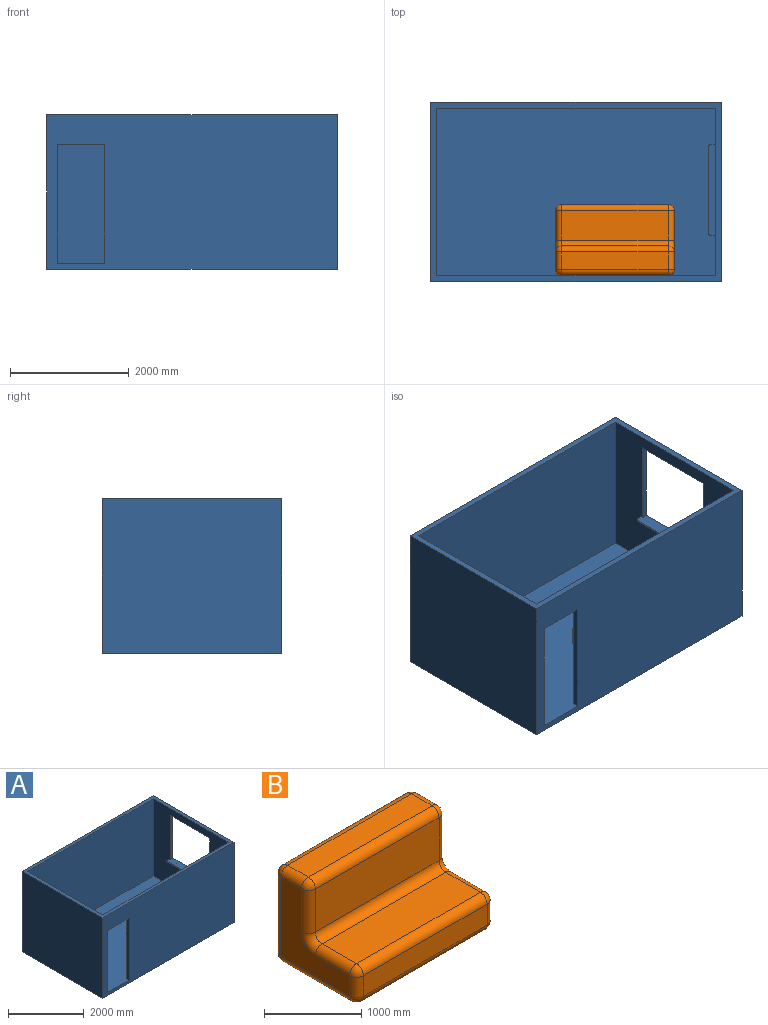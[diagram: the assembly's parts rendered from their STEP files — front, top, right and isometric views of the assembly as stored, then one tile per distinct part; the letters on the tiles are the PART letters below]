
ASSEMBLY  parts=2 mates=2
PART A: 24 faces, bbox 4900x3020x2600 mm
  f0: plane 2820x2500mm, normal (-1,0,0), area 4899320mm2, adj f2,f6,f8,f9,f14,f15,f16,f17
  f1: plane 4900x2600mm, normal (0,-1,0), area 11140000mm2, adj f3,f4,f8,f9,f10,f11,f12,f13
  f2: plane 4700x2500mm, normal (0,1,0), area 10150000mm2, adj f0,f5,f8,f9,f11,f12,f13
  f3: plane 3020x2600mm, normal (-1,0,0), area 7852000mm2, adj f1,f7,f8,f10
  f4: plane 3020x2600mm, normal (1,0,0), area 5735200mm2, adj f1,f7,f8,f10,f14,f15,f16,f17
  f5: plane 2820x2500mm, normal (1,0,0), area 7050000mm2, adj f2,f6,f8,f9
  f6: plane 4700x2500mm, normal (0,-1,0), area 11750000mm2, adj f0,f5,f8,f9
  f7: plane 4900x2600mm, normal (0,1,0), area 12740000mm2, adj f3,f4,f8,f10
  f8: plane 4900x3020mm, normal (0,0,1), area 1544000mm2, adj f0,f1,f2,f3,f4,f5,f6,f7
  f9: plane 4700x2920mm, normal (0,0,1), area 13334000mm2, adj f0,f1,f2,f5,f6,f11,f12
  f10: plane 4900x3020mm, normal (0,0,-1), area 14798000mm2, adj f1,f3,f4,f7
  f11: plane 2000x100mm, normal (1,0,0), area 200000mm2, adj f1,f2,f9,f13
  f12: plane 2000x100mm, normal (-1,0,0), area 200000mm2, adj f1,f2,f9,f13
  f13: plane 800x100mm, normal (0,0,-1), area 80000mm2, adj f1,f2,f11,f12
  f14: plane 1440x100mm, normal (0,-1,0), area 144000mm2, adj f0,f4,f15,f17
  f15: plane 1540x210mm, normal (0,0,1), area 315874.2mm2, adj f0,f4,f14,f16,f18,f20,f21,f22
  f16: plane 1440x100mm, normal (0,1,0), area 144000mm2, adj f0,f4,f15,f17
  f17: plane 1470x100mm, normal (0,0,-1), area 147000mm2, adj f0,f4,f14,f16
  f18: plane 75x22mm, normal (0,1,0), area 1650mm2, adj f0,f15,f19,f22
  f19: plane 1540x110mm, normal (0,0,-1), area 168874.2mm2, adj f0,f18,f20,f21,f22,f23
  f20: plane 75x22mm, normal (0,-1,0), area 1650mm2, adj f0,f15,f19,f23
  f21: plane 1470x22mm, normal (-1,0,0), area 32340mm2, adj f15,f19,f22,f23
  f22: cylinder r=35mm len=35mm, axis (0,0,1), area 1209.5mm2, adj f15,f18,f19,f21
  f23: cylinder r=35mm len=35mm, axis (0,0,-1), area 1209.5mm2, adj f15,f19,f20,f21
PART B: 38 faces, bbox 2000x1200x1200 mm
  f0: plane 1000x1000mm, normal (1,0,0), area 490584.1mm2, adj f8,f12,f13,f22,f23,f24,f28
  f1: plane 1800x300mm, normal (0,0,1), area 540000mm2, adj f11,f12,f20,f21
  f2: plane 1800x260mm, normal (0,-1,0), area 468000mm2, adj f24,f25,f33,f34
  f3: plane 1800x1000mm, normal (0,1,0), area 1800000mm2, adj f8,f11,f14,f15
  f4: plane 1000x1000mm, normal (-1,0,0), area 490584.1mm2, adj f15,f20,f26,f31,f34,f35,f37
  f5: plane 1800x1000mm, normal (0,0,-1), area 1800000mm2, adj f13,f14,f25,f26
  f6: plane 1800x500mm, normal (0,0,1), area 900000mm2, adj f23,f32,f33,f37
  f7: plane 1800x540mm, normal (0,-1,0), area 972000mm2, adj f21,f22,f31,f32
  f8: cylinder r=100mm len=1000mm, axis (0,0,-1), area 157079.6mm2, adj f0,f3,f9,f10
  f9: sphere r=100mm, area 15708mm2, adj f8,f11,f12
  f10: sphere r=100mm, area 15708mm2, adj f8,f13,f14
  f11: cylinder r=100mm len=1800mm, axis (1,0,0), area 282743.3mm2, adj f1,f3,f9,f16
  f12: cylinder r=100mm len=300mm, axis (0,-1,0), area 47123.9mm2, adj f0,f1,f9,f17
  f13: cylinder r=100mm len=1000mm, axis (0,1,0), area 157079.6mm2, adj f0,f5,f10,f18
  f14: cylinder r=100mm len=1800mm, axis (-1,0,0), area 282743.3mm2, adj f3,f5,f10,f19
  f15: cylinder r=100mm len=1000mm, axis (0,0,1), area 157079.6mm2, adj f3,f4,f16,f19
  f16: sphere r=100mm, area 15708mm2, adj f11,f15,f20
  f17: sphere r=100mm, area 15708mm2, adj f12,f21,f22
  f18: sphere r=100mm, area 15708mm2, adj f13,f24,f25
  f19: sphere r=100mm, area 15708mm2, adj f14,f15,f26
  f20: cylinder r=100mm len=300mm, axis (0,1,0), area 47123.9mm2, adj f1,f4,f16,f27
  f21: cylinder r=100mm len=1800mm, axis (1,0,0), area 282743.3mm2, adj f1,f7,f17,f27
  f22: cylinder r=100mm len=540mm, axis (0,0,1), area 84823mm2, adj f0,f7,f17,f28
  f23: cylinder r=100mm len=500mm, axis (0,1,0), area 78539.8mm2, adj f0,f6,f28,f29
  f24: cylinder r=100mm len=260mm, axis (0,0,1), area 40840.7mm2, adj f0,f2,f18,f29
  f25: cylinder r=100mm len=1800mm, axis (1,0,0), area 282743.3mm2, adj f2,f5,f18,f30
  f26: cylinder r=100mm len=1000mm, axis (0,-1,0), area 157079.6mm2, adj f4,f5,f19,f30
  f27: sphere r=100mm, area 15708mm2, adj f20,f21,f31
  f28: torus R=200mm, axis (-1,0,0), area 33640.1mm2, adj f0,f22,f23,f32
  f29: sphere r=100mm, area 15708mm2, adj f23,f24,f33
  f30: sphere r=100mm, area 15708mm2, adj f25,f26,f34
  f31: cylinder r=100mm len=540mm, axis (0,0,1), area 84823mm2, adj f4,f7,f27,f35
  f32: cylinder r=100mm len=1800mm, axis (1,0,0), area 282743.3mm2, adj f6,f7,f28,f35
  f33: cylinder r=100mm len=1800mm, axis (-1,0,0), area 282743.3mm2, adj f2,f6,f29,f36
  f34: cylinder r=100mm len=260mm, axis (0,0,-1), area 40840.7mm2, adj f2,f4,f30,f36
  f35: torus R=200mm, axis (-1,0,0), area 33640.1mm2, adj f4,f31,f32,f37
  f36: sphere r=100mm, area 15708mm2, adj f33,f34,f37
  f37: cylinder r=100mm len=500mm, axis (0,1,0), area 78539.8mm2, adj f4,f6,f35,f36
PLACE A t=(-1776.13,-1501.65,307.69)mm fixed
PLACE B rot(axis=(0,0,1),180deg) t=(-1120.85,-2311.65,907.69)mm
MATE planar B.f5 <-> A.f9  axis (0,0,-1) through (-1120.85,-2311.65,307.69)mm
MATE planar B.f3 <-> A.f2  axis (0,-1,0) through (-1120.85,-2911.65,907.69)mm
